FCSTD DOCUMENT  (FreeCAD 2021.911R24301 +3846 (Git))
Label: top mount
License: All rights reserved
LicenseURL: http://en.wikipedia.org/wiki/All_rights_reserved
objects: Sketcher::SketchObject×5, PartDesign::Pad×4, PartDesign::Body×3, Part::Part2DObjectPython×2, PartDesign::AdditiveHelix×1, PartDesign::Pocket×1, PartDesign::SubtractiveHelix×1, PartDesign::Hole×1, PartDesign::Chamfer×1
note: 37 computed .brp shape members not serialized (recipe doc carries the construction recipe); baked Part::Feature solids carry a one-line shape summary decoded from their .brp

FEATURE [Sketcher::SketchObject] Sketch
  FullyConstrained = true
  MapMode = 5
  Support = -> [XY_Plane]
  sketch-geometry (1):
    g0: Circle CenterX=0 CenterY=0 CenterZ=0 NormalX=0 NormalY=0 NormalZ=1 AngleXU=0 Radius=35
  constraints (2):
    c: Coincident(g0,g-1)
    c: Diameter(g0) = 70
FEATURE [PartDesign::Pad] Pad
  ClaimChildren = false
  Direction = (1,1,1)
  Fit = 0
  FitJoin = 0
  InnerFit = 0
  InnerFitJoin = 0
  InnerTaperAngle = 0
  InnerTaperAngleRev = 0
  Length = 10
  Length2 = 100
  Linearize = true
  NewSolid = false
  Profile = -> Sketch
  Refine = true
  Suppress = false
  Type = 0
  _ProfileBasedVersion = 1
FEATURE [Part::Part2DObjectPython] VThreadProfile  # Draft 2D object (typed FeaturePython)
  Area = 1343.86
  Closed = true
  Continuity = C3
  Instructions = Expand this with the ... button to view instructions | Sweep this object along a helix of the same pitch to produce your thread. | It is recommended to make the helix in the ThreadProfile workbench. | If there is an active Body the ThreadProfile object will be put into it.,If not it can be dragged and dropped into the body later. | If there is an active Body when the helix is made there will be made a ShapeBinder for it | For internal threads you will need to cut the Sweep object out of a cylinder, or if using Part Design sweep it as a Subtractive Pipe. | Always use Frenet mode | I have provided some presets, but it is possible there could be some errors.  Double check for mission critical applications. | Also, the tolerances might be different from what you wish to have.  I believe the internal minor diameters are all minimum and the external are all maximum.
  InternalOrExternal = 1
  MakeFace = true
  MinorDiameter = 40
  Parameterization = 1
  Pitch = 3
  Placement = pos=(0,0,10) rot=(0,0,1;0rad)
  Points = (719) [(19.9922,0.174712,0),(19.9831,0.349292,0),(19.9728,0.523734,0),(19.9612,0.698031,0),(19.9483,0.872175,0),(19.9341,1.04616,0),(19.9186,1.21997,0),+712 more]
  Presets = 0
  Quality = 1
  ThreadCount = 10
  Version = 1.69
  external_data = [-0.00235387,-0.00461052,-0.00677828,-0.00886428,-0.0108747,-0.0128149,-0.0146895,-0.0165028,-0.0182584,-0.0199597,-0.0216095,-0.0232106,-0.0247653,-0.0262759,-0.0277444,-0.0291725,-0.0305621,-0.0319145,-0.0332313,-0.0345138,-0.0357632,+698 more]
  internal_data = [0,0,0,0,0,0,0,0,0,0,0,0,0,0,0,0,0,0,0,0,0,0,0,0,0,0,0,0,0,0,0,0,0,0,0,0,0,0,0,0,0,0,0,0,0,0,0,0,0,0,0,0,0,0,0,0,0,0,0,0,0,0,0,0,0,0,0,0,0,0,0,0,0,0,0,0,0,0,0,0,0,0,0,0,0,0,0,0,0,0,0,0,0,0,0,0,0,0,0,0,0,0,0,0,0,0,0,0,0,0,0,0,0,0,0,0,0,0,0,0,+599 more]
  preset_names = <blob: 3959 chars omitted>
  presets_data = [0,0,0,2.20878,24.1173,24.6888,0.25,0.693,0.729,0.25,0.793,0.829,0.25,0.893,0.929,0.3,1.032,1.075,0.35,1.171,1.221,0.35,1.371,1.421,0.4,1.509,1.567,0.45,1.648,1.713,0.45,1.948,2.013,0.5,2.387,2.459,0.6,2.764,2.85,0.7,3.141,3.242,0.75,3.58,+712 more]
FEATURE [PartDesign::AdditiveHelix] AdditiveHelix
  Angle = 0
  Axis = (-3e-16,3e-16,1)
  Base = (0,0,0)
  BaseFeature = -> Pad
  ClaimChildren = false
  Fit = 0
  FitJoin = 0
  HasBeenEdited = true
  Height = 30
  InnerFit = 0
  InnerFitJoin = 0
  LeftHanded = false
  Mode = 0
  NewSolid = false
  Outside = false
  Pitch = 3
  Profile = -> VThreadProfile
  ReferenceAxis = -> Z_Axis
  Refine = true
  Suppress = false
  Turns = 3
  _ProfileBasedVersion = 1
FEATURE [Sketcher::SketchObject] Sketch001
  FullyConstrained = true
  MapMode = 5
  Placement = pos=(0,0,0) rot=(1,0,0;3.14159rad)
  Support = -> [AdditiveHelix]
  sketch-geometry (1):
    g0: Circle CenterX=0 CenterY=0 CenterZ=0 NormalX=0 NormalY=0 NormalZ=1 AngleXU=0 Radius=14.5
  constraints (2):
    c: Coincident(g0,g-1)
    c: Diameter(g0) = 29
FEATURE [PartDesign::Pocket] Pocket
  BaseFeature = -> AdditiveHelix
  ClaimChildren = false
  Fit = 0
  FitJoin = 0
  InnerFit = 0
  InnerFitJoin = 0
  InnerTaperAngle = 0
  InnerTaperAngleRev = 0
  Length = 30
  Length2 = 100
  Linearize = true
  NewSolid = false
  Profile = -> Sketch001
  Refine = true
  Suppress = false
  Type = 0
  _ProfileBasedVersion = 1
FEATURE [PartDesign::Body] Body  label="leg cap top"
  AutoGroupSolids = false
  ExportMode = 0
  Group = -> [Sketch,Pad,VThreadProfile,AdditiveHelix,Sketch001,Pocket]
  Origin = -> Origin
  Tip = -> Pocket
  _ExportChildren = -> [Pad,AdditiveHelix,Pocket]
  _GroupVersion = 1
FEATURE [Sketcher::SketchObject] Sketch002
  FullyConstrained = false
  MapMode = 5
  Support = -> [XY_Plane002]
  sketch-geometry (24):
    g0: LineSegment [constr] StartX=-35 StartY=35 StartZ=0 EndX=35 EndY=35 EndZ=0
    g1: LineSegment [constr] StartX=35 StartY=35 StartZ=0 EndX=35 EndY=-35 EndZ=0
    g2: LineSegment [constr] StartX=35 StartY=-35 StartZ=0 EndX=-35 EndY=-35 EndZ=0
    g3: LineSegment [constr] StartX=-35 StartY=-35 StartZ=0 EndX=-35 EndY=35 EndZ=0
    g4: LineSegment StartX=35 StartY=-13.9841 StartZ=0 EndX=35 EndY=13.9841 EndZ=0
    g5: LineSegment StartX=30 StartY=22.6443 StartZ=0 EndX=16.0466 EndY=30.7003 EndZ=0
    g6: LineSegment StartX=-16.0466 StartY=30.7003 StartZ=0 EndX=-30 EndY=22.6443 EndZ=0
    g7: LineSegment StartX=-35 StartY=13.9841 StartZ=0 EndX=-35 EndY=-13.9841 EndZ=0
    g8: LineSegment StartX=-30 StartY=-22.6443 StartZ=0 EndX=-16.0466 EndY=-30.7003 EndZ=0
    g9: LineSegment StartX=16.0466 StartY=-30.7003 StartZ=0 EndX=30 EndY=-22.6443 EndZ=0
    g10: Circle [constr] CenterX=0 CenterY=0 CenterZ=0 NormalX=0 NormalY=0 NormalZ=1 AngleXU=0 Radius=33.4861
    g11: ArcOfCircle CenterX=-25 CenterY=13.9841 CenterZ=0 NormalX=0 NormalY=0 NormalZ=1 AngleXU=0 Radius=10 StartAngle=2.0944 EndAngle=3.14159
    g12: ArcOfCircle CenterX=25 CenterY=13.9841 CenterZ=0 NormalX=0 NormalY=0 NormalZ=1 AngleXU=0 Radius=10 StartAngle=1e-16 EndAngle=1.0472
    g13: ArcOfCircle CenterX=25 CenterY=-13.9841 CenterZ=0 NormalX=0 NormalY=0 NormalZ=1 AngleXU=0 Radius=10 StartAngle=5.23599 EndAngle=6.28319
    g14: ArcOfCircle CenterX=-25 CenterY=-13.9841 CenterZ=0 NormalX=0 NormalY=0 NormalZ=1 AngleXU=0 Radius=10 StartAngle=3.14159 EndAngle=4.18879
    g15: ArcOfCircle CenterX=-2e-15 CenterY=-2.90673 CenterZ=0 NormalX=0 NormalY=0 NormalZ=1 AngleXU=0 Radius=32.0933 StartAngle=4.18879 EndAngle=5.23599
    g16: ArcOfCircle CenterX=2.1e-15 CenterY=2.90673 CenterZ=0 NormalX=0 NormalY=0 NormalZ=1 AngleXU=0 Radius=32.0933 StartAngle=1.0472 EndAngle=2.0944
    g17: Circle CenterX=-25 CenterY=13.9841 CenterZ=0 NormalX=0 NormalY=0 NormalZ=1 AngleXU=0 Radius=1
    g18: Circle CenterX=25 CenterY=13.9841 CenterZ=0 NormalX=0 NormalY=0 NormalZ=1 AngleXU=0 Radius=1
    g19: LineSegment [constr] StartX=25 StartY=13.9841 StartZ=0 EndX=-25 EndY=13.9841 EndZ=0
    g20: LineSegment [constr] StartX=-25 StartY=13.9841 StartZ=0 EndX=0 EndY=-29.3172 EndZ=0
    g21: LineSegment [constr] StartX=0 StartY=-29.3172 StartZ=0 EndX=25 EndY=13.9841 EndZ=0
    g22: Circle [constr] CenterX=-4e-16 CenterY=-0.449673 CenterZ=0 NormalX=0 NormalY=0 NormalZ=1 AngleXU=0 Radius=28.8675
    g23: Circle CenterX=0 CenterY=-29.3172 CenterZ=0 NormalX=0 NormalY=0 NormalZ=1 AngleXU=0 Radius=1
  constraints (56):
    c: Coincident(g0,g1)
    c: Coincident(g1,g2)
    c: Coincident(g2,g3)
    c: Coincident(g3,g0)
    c: Horizontal(g0)
    c: Horizontal(g2)
    c: Vertical(g1)
    c: Vertical(g3)
    c: DistanceX(g2,g2) = 70
    c: Symmetric(g1,g0,g-1)
    c: Vertical(g7)
    c: Coincident(g-1,g10)
    c: Tangent(g7,g11) = -1.5708
    c: Tangent(g6,g11) = -1.5708
    c: Tangent(g5,g12) = -1.5708
    c: Tangent(g4,g12) = -1.5708
    c: Tangent(g4,g13) = -1.5708
    c: Tangent(g9,g13) = -1.5708
    c: Tangent(g8,g14) = -1.5708
    c: Tangent(g7,g14) = -1.5708
    c: Tangent(g8,g15) = -1.5708
    c: Tangent(g9,g15) = -1.5708
    c: Tangent(g6,g16) = -1.5708
    c: Tangent(g5,g16) = -1.5708
    c: Angle(g9) = 0.523599
    c: Angle(g8) = -0.523599
    c: Angle(g6) = -2.61799
    c: Angle(g5) = 2.61799
    c: Vertical(g4,g0)
    c: Vertical(g7,g0)
    c: Horizontal(g7,g4)
    c: Equal(g4,g7)
    c: Equal(g5,g9)
    c: Equal(g9,g8)
    c: Symmetric(g4,g4,g-1)
    c: Tangent(g16,g0)
    c: Equal(g0,g1)
    c: Tangent(g15,g2)
    c: Equal(g12,g11)
    c: Diameter(g12) = 20
    c: Coincident(g17,g11)
    c: Coincident(g18,g12)
    c: Coincident(g19,g20)
    c: Coincident(g20,g21)
    c: Coincident(g21,g19)
    c: Equal(g19,g20)
    c: Equal(g19,g21)
    c: PointOnObject(g19,g22)
    c: PointOnObject(g20,g22)
    c: PointOnObject(g21,g22)
    c: Coincident(g21,g12)
    c: Coincident(g19,g11)
    c: Coincident(g23,g20)
    c: Diameter(g23) = 2
    c: Equal(g23,g17)
    c: Equal(g23,g18)
FEATURE [PartDesign::Pad] Pad001
  ClaimChildren = false
  Direction = (1,1,1)
  Fit = 0
  FitJoin = 0
  InnerFit = 0
  InnerFitJoin = 0
  InnerTaperAngle = 0
  InnerTaperAngleRev = 0
  Length = 10
  Length2 = 100
  Linearize = true
  NewSolid = false
  Profile = -> Sketch002
  Refine = true
  Suppress = false
  Type = 0
  _ProfileBasedVersion = 1
FEATURE [Part::Part2DObjectPython] VThreadProfile001  # Draft 2D object (typed FeaturePython)
  Area = 1349.3
  AttachmentOffset = pos=(0,0,1) rot=(0,0,1;0rad)
  Closed = true
  Continuity = C3
  Instructions = Expand this with the ... button to view instructions | Sweep this object along a helix of the same pitch to produce your thread. | It is recommended to make the helix in the ThreadProfile workbench. | If there is an active Body the ThreadProfile object will be put into it.,If not it can be dragged and dropped into the body later. | If there is an active Body when the helix is made there will be made a ShapeBinder for it | For internal threads you will need to cut the Sweep object out of a cylinder, or if using Part Design sweep it as a Subtractive Pipe. | Always use Frenet mode | I have provided some presets, but it is possible there could be some errors.  Double check for mission critical applications. | Also, the tolerances might be different from what you wish to have.  I believe the internal minor diameters are all minimum and the external are all maximum.
  InternalOrExternal = 0
  MakeFace = true
  MapMode = 5
  MinorDiameter = 40
  Parameterization = 1
  Pitch = 3
  Placement = pos=(0,0,11) rot=(0,0,1;0rad)
  Points = (719) [(19.9992,0.174773,0),(19.9969,0.349534,0),(19.9931,0.524267,0),(19.9878,0.69896,0),(19.9809,0.8736,0),(19.9725,1.04817,0),(19.9626,1.22267,0),+712 more]
  Presets = 0
  Quality = 1
  Support = -> [Pad001]
  ThreadCount = 10
  Version = 1.69
  external_data = [-0.00235387,-0.00461052,-0.00677828,-0.00886428,-0.0108747,-0.0128149,-0.0146895,-0.0165028,-0.0182584,-0.0199597,-0.0216095,-0.0232106,-0.0247653,-0.0262759,-0.0277444,-0.0291725,-0.0305621,-0.0319145,-0.0332313,-0.0345138,-0.0357632,+698 more]
  internal_data = [0,0,0,0,0,0,0,0,0,0,0,0,0,0,0,0,0,0,0,0,0,0,0,0,0,0,0,0,0,0,0,0,0,0,0,0,0,0,0,0,0,0,0,0,0,0,0,0,0,0,0,0,0,0,0,0,0,0,0,0,0,0,0,0,0,0,0,0,0,0,0,0,0,0,0,0,0,0,0,0,0,0,0,0,0,0,0,0,0,0,0,0,0,0,0,0,0,0,0,0,0,0,0,0,0,0,0,0,0,0,0,0,0,0,0,0,0,0,0,0,+599 more]
  preset_names = <blob: 3959 chars omitted>
  presets_data = [0,0,0,2.20878,24.1173,24.6888,0.25,0.693,0.729,0.25,0.793,0.829,0.25,0.893,0.929,0.3,1.032,1.075,0.35,1.171,1.221,0.35,1.371,1.421,0.4,1.509,1.567,0.45,1.648,1.713,0.45,1.948,2.013,0.5,2.387,2.459,0.6,2.764,2.85,0.7,3.141,3.242,0.75,3.58,+712 more]
FEATURE [Sketcher::SketchObject] Sketch003
  FullyConstrained = true
  MapMode = 5
  Placement = pos=(0,0,0) rot=(1,0,0;3.14159rad)
  Support = -> [Pad001]
  sketch-geometry (1):
    g0: Circle CenterX=0 CenterY=0 CenterZ=0 NormalX=0 NormalY=0 NormalZ=1 AngleXU=0 Radius=25
  constraints (2):
    c: Coincident(g0,g-1)
    c: Diameter(g0) = 50
FEATURE [PartDesign::Pad] Pad002
  BaseFeature = -> Pad001
  ClaimChildren = false
  Direction = (1,1,1)
  Fit = 0
  FitJoin = 0
  InnerFit = 0
  InnerFitJoin = 0
  InnerTaperAngle = 0
  InnerTaperAngleRev = 0
  Length = 18
  Length2 = 100
  Linearize = true
  NewSolid = false
  Profile = -> Sketch003
  Refine = true
  Suppress = false
  Type = 0
  _ProfileBasedVersion = 1
FEATURE [PartDesign::SubtractiveHelix] SubtractiveHelix
  Angle = 0
  Axis = (-3e-16,3e-16,1)
  Base = (0,0,0)
  BaseFeature = -> Pad002
  ClaimChildren = false
  Fit = 0.5
  FitJoin = 0
  HasBeenEdited = true
  Height = 35
  InnerFit = 0
  InnerFitJoin = 0
  LeftHanded = false
  Mode = 0
  NewSolid = false
  Outside = false
  Pitch = 3
  Profile = -> VThreadProfile001
  ReferenceAxis = -> Z_Axis002
  Refine = true
  Reversed = true
  Suppress = false
  Turns = 3
  _ProfileBasedVersion = 1
FEATURE [Sketcher::SketchObject] Sketch004
  FullyConstrained = true
  MapMode = 5
  Support = -> [XY_Plane003]
  sketch-geometry (2):
    g0: Circle CenterX=0 CenterY=0 CenterZ=0 NormalX=0 NormalY=0 NormalZ=1 AngleXU=0 Radius=35
    g1: Circle CenterX=0 CenterY=0 CenterZ=0 NormalX=0 NormalY=0 NormalZ=1 AngleXU=0 Radius=23.5
  constraints (4):
    c: Coincident(g0,g-1)
    c: Diameter(g0) = 70
    c: Coincident(g1,g0)
    c: Diameter(g1) = 47
FEATURE [PartDesign::Pad] Pad003
  ClaimChildren = false
  Direction = (1,1,1)
  Fit = 0
  FitJoin = 0
  InnerFit = 0
  InnerFitJoin = 0
  InnerTaperAngle = 0
  InnerTaperAngleRev = 0
  Length = 2
  Length2 = 100
  Linearize = true
  NewSolid = false
  Profile = -> Sketch004
  Refine = true
  Suppress = false
  Type = 0
  _ProfileBasedVersion = 1
FEATURE [PartDesign::Body] Body003  label="dampener"
  AutoGroupSolids = false
  ExportMode = 0
  Group = -> [Sketch004,Pad003]
  Origin = -> Origin003
  Placement = pos=(0,-1.19209e-06,10) rot=(0,0,1;0rad)
  Tip = -> Pad003
  _ExportChildren = -> [Pad003]
  _GroupVersion = 1
FEATURE [PartDesign::Hole] Hole
  BaseFeature = -> SubtractiveHelix
  ClaimChildren = false
  CustomThreadClearance = 0
  Depth = 25
  DepthType = 1
  Diameter = 4
  DrillForDepth = false
  DrillPoint = 1
  DrillPointAngle = 118
  Fit = 0
  FitJoin = 0
  HoleCutCountersinkAngle = 90
  HoleCutCustomValues = false
  HoleCutDepth = 0
  HoleCutDiameter = 8
  HoleCutType = 2
  InnerFit = 0
  InnerFitJoin = 0
  ModelThread = false
  NewSolid = false
  Profile = -> SubtractiveHelix [Edge33,Edge117,Edge116]
  Refine = true
  Suppress = false
  Tapered = false
  TaperedAngle = 90
  ThreadClass = 0
  ThreadDepth = 207.81
  ThreadDepthType = 0
  ThreadDirection = 0
  ThreadFit = 0
  ThreadSize = 0
  ThreadType = 0
  Threaded = false
  UseCustomThreadClearance = false
  _ProfileBasedVersion = 1
FEATURE [PartDesign::Chamfer] Chamfer
  Angle = 45
  Base = -> Hole [Edge26]
  BaseFeature = -> Hole
  ChamferType = 0
  FlipDirection = false
  NewSolid = false
  Refine = true
  Size = 1
  Size2 = 1
  SupportTransform = false
  Suppress = false
FEATURE [PartDesign::Body] Body002  label="table mount"
  AutoGroupSolids = false
  ExportMode = 0
  Group = -> [Sketch002,Pad001,VThreadProfile001,Sketch003,Pad002,SubtractiveHelix,Hole,Chamfer]
  Origin = -> Origin002
  Placement = pos=(0,-3.57628e-06,30) rot=(0,0,1;0rad)
  Tip = -> Chamfer
  _ExportChildren = -> [Pad001,Pad002,Hole,Chamfer]
  _GroupVersion = 1
